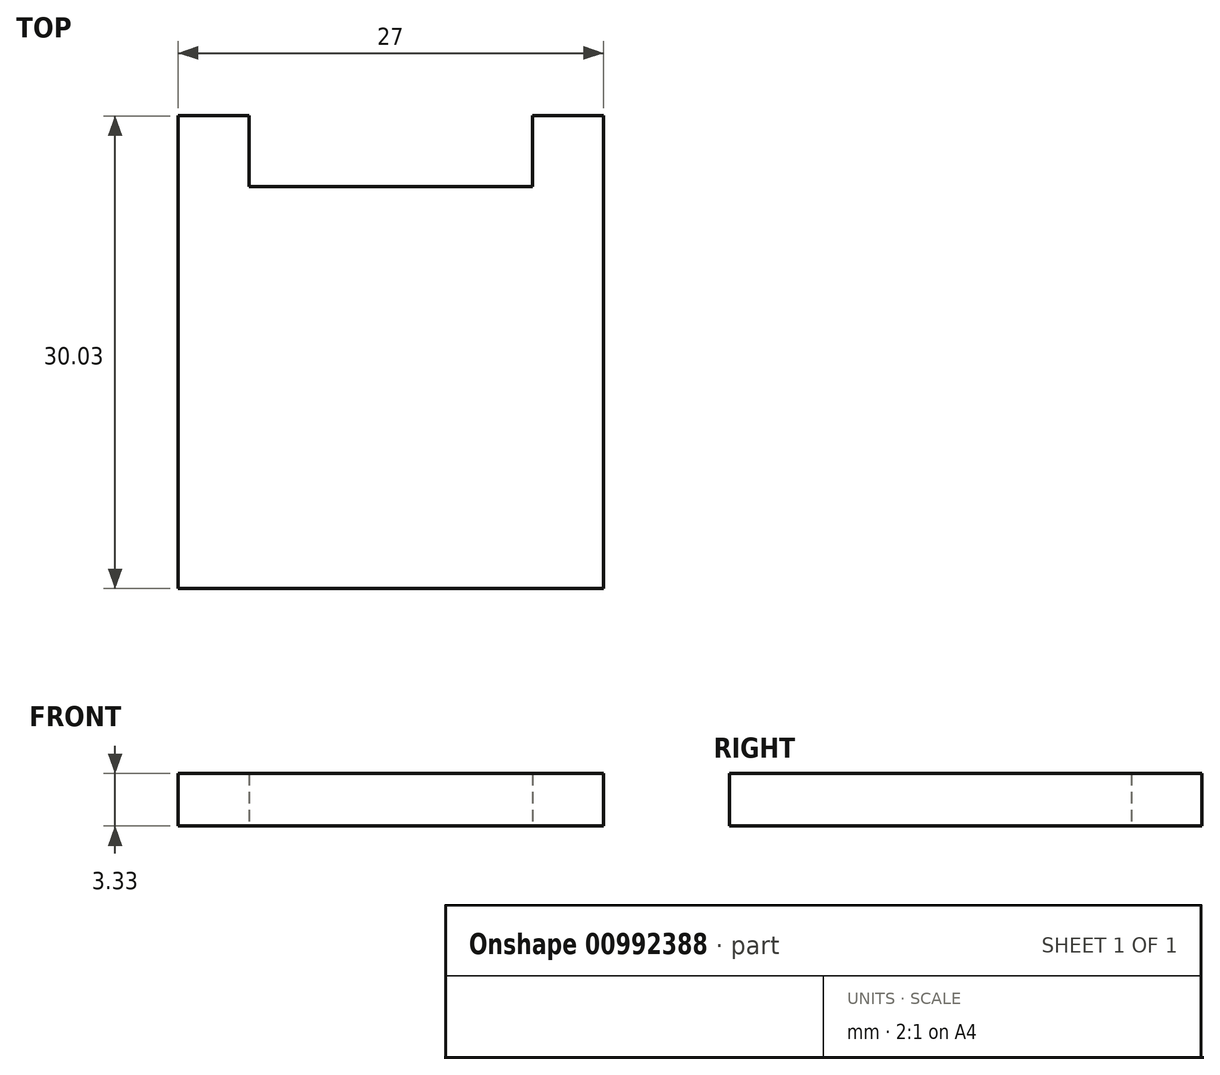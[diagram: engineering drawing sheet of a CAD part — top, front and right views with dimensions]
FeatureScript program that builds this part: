
annotation { "Feature Type Name" : "Feature", "Feature Type Description" : "" }
export const myFeature = defineFeature(function(context is Context, id is Id, definition is map)
    precondition{}
    {
        {
            var Q0;
            Q0=qCreatedBy(makeId("Top.planeOp"),FACE);
            var sketch = newSketch(context, id + "F0", { "sketchPlane" : qUnion([Q0])});
            skLineSegment(sketch, "E0.bottom", {"start": v(-46.26, 52.32) * mm, "end": v(-28.26, 52.32) * mm});
            skLineSegment(sketch, "E0.top", {"start": v(-46.26, 31.3) * mm, "end": v(-28.26, 31.3) * mm, "construction": true});
            skLineSegment(sketch, "E0.left", {"start": v(-46.26, 56.82) * mm, "end": v(-46.26, 26.8) * mm});
            skLineSegment(sketch, "E0.right", {"start": v(-28.26, 56.82) * mm, "end": v(-28.26, 26.8) * mm});
            skLineSegment(sketch, "E1.0", {"start": v(-23.76, 56.82) * mm, "end": v(-23.76, 26.8) * mm});
            skLineSegment(sketch, "E1.1", {"start": v(-50.76, 56.82) * mm, "end": v(-23.76, 56.82) * mm});
            skLineSegment(sketch, "E1.2", {"start": v(-50.76, 56.82) * mm, "end": v(-50.76, 26.8) * mm});
            skLineSegment(sketch, "E1.3", {"start": v(-50.76, 26.8) * mm, "end": v(-23.76, 26.8) * mm});
            skSolve(sketch);
        }
        {
            var Q0;
            {var subQ0=sQuery(id+"F0.wireOp",EDGE,"E1.2");Q0=makeQuery(id+"F0.imprint","IMPRINT",FACE,{"disambiguationData":[TD([[makeQuery(id+"F0.imprint","IMPRINT",EDGE,{"derivedFrom":subQ0}),1.0]])]});}
            var Q1;
            {var subQ0=sQuery(id+"F0.wireOp",EDGE,"E0.bottom");Q1=makeQuery(id+"F0.imprint","IMPRINT",FACE,{"disambiguationData":[TD([[makeQuery(id+"F0.imprint","IMPRINT",EDGE,{"derivedFrom":subQ0}),-1.0]])]});}
            var Q2;
            {var subQ0=sQuery(id+"F0.wireOp",EDGE,"E1.0");Q2=makeQuery(id+"F0.imprint","IMPRINT",FACE,{"disambiguationData":[TD([[makeQuery(id+"F0.imprint","IMPRINT",EDGE,{"derivedFrom":subQ0}),-1.0]])]});}
            extrude(context, id + "F1", {"entities" : qUnion([Q0, Q1, Q2]), "depth" : 3.33 * mm, "offsetDistance" : 25 * mm});
        }
    });
